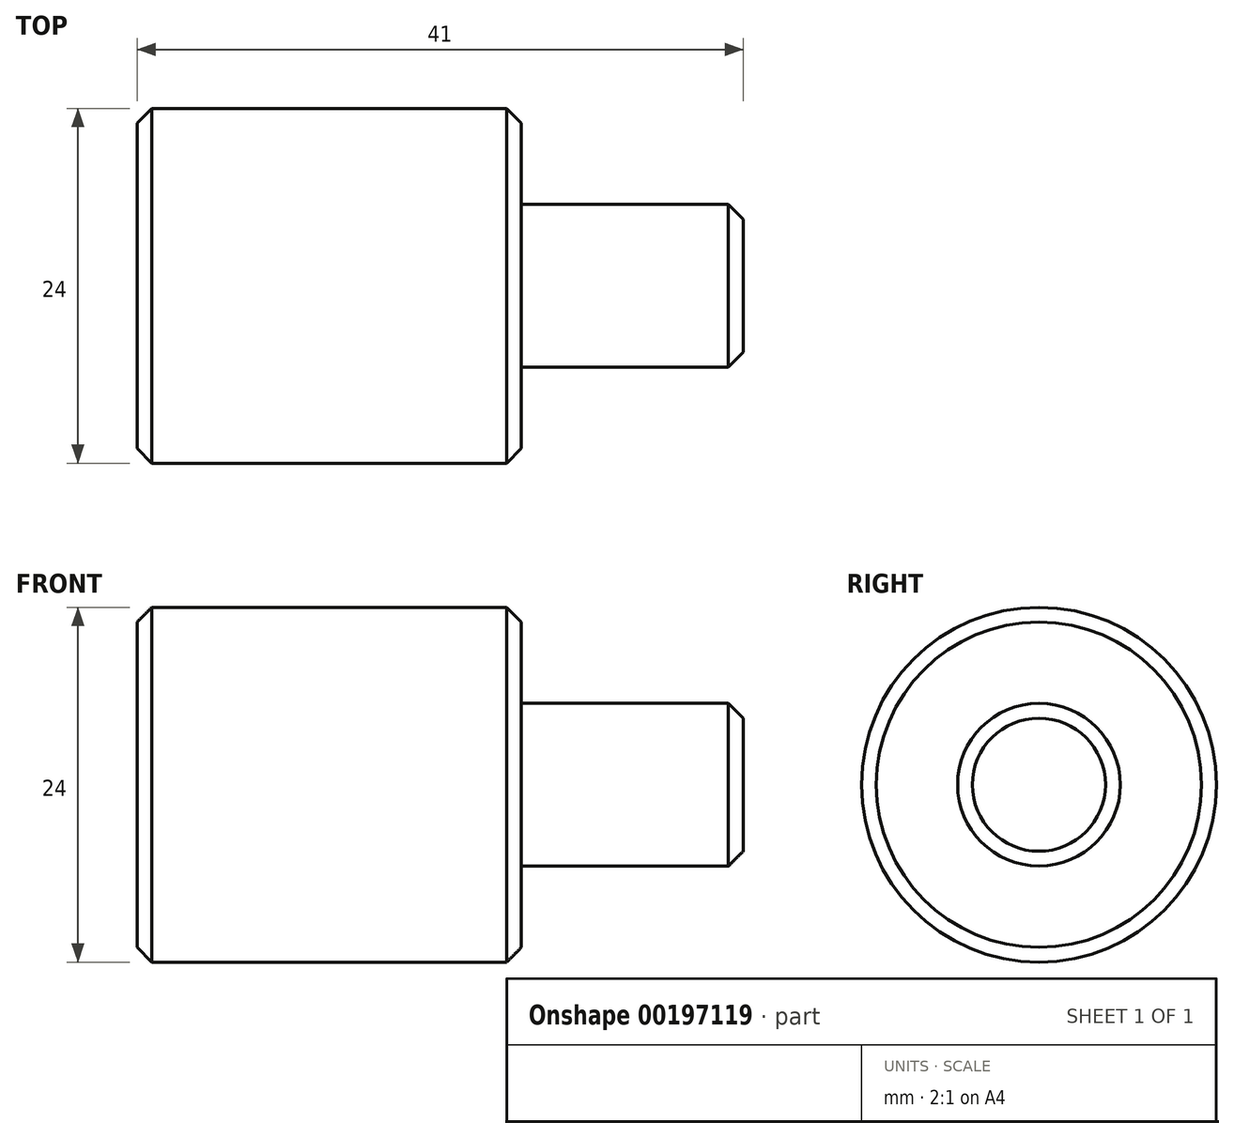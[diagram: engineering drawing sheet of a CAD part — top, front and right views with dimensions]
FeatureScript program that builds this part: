
annotation { "Feature Type Name" : "Feature", "Feature Type Description" : "" }
export const myFeature = defineFeature(function(context is Context, id is Id, definition is map)
    precondition{}
    {
        {
            var Q0;
            Q0=qCreatedBy(makeId("Front.planeOp"),FACE);
            var sketch = newSketch(context, id + "F0", { "sketchPlane" : qUnion([Q0])});
            skLineSegment(sketch, "E0", {"start": v(-12.2, 0) * mm, "end": v(50.6, 0) * mm, "construction": true});
            skLineSegment(sketch, "E1", {"start": v(0, 0) * mm, "end": v(0, 12) * mm});
            skLineSegment(sketch, "E2", {"start": v(0, 12) * mm, "end": v(26, 12) * mm});
            skLineSegment(sketch, "E3", {"start": v(26, 12) * mm, "end": v(26, 5.5) * mm});
            skLineSegment(sketch, "E4", {"start": v(26, 5.5) * mm, "end": v(41, 5.5) * mm});
            skLineSegment(sketch, "E5", {"start": v(41, 5.5) * mm, "end": v(41, 0) * mm});
            skLineSegment(sketch, "E6", {"start": v(41, 0) * mm, "end": v(0, 0) * mm});
            skSolve(sketch);
        }
        {
            var Q0;
            Q0 = qSketchRegion(id + "F0", true);
            var Q1;
            Q1=sQuery(id+"F0.wireOp",EDGE,"E0");
            revolve(context, id + "F1", {"entities" : qUnion([Q0]), "axis" : qUnion([Q1]), "revolveType" : RevolveType.FULL});
        }
        {
            var Q0;
            Q0=makeQuery(id+"F1.opRevolve","SWEPT_EDGE",EDGE,{"disambiguationData":[OSD([sQuery(id+"F0.wireOp",EDGE,"E1"),sQuery(id+"F0.wireOp",EDGE,"E2")])]});
            var Q1;
            Q1=makeQuery(id+"F1.opRevolve","SWEPT_EDGE",EDGE,{"disambiguationData":[OSD([sQuery(id+"F0.wireOp",EDGE,"E2"),sQuery(id+"F0.wireOp",EDGE,"E3")])]});
            var Q2;
            Q2=makeQuery(id+"F1.opRevolve","SWEPT_EDGE",EDGE,{"disambiguationData":[OSD([sQuery(id+"F0.wireOp",EDGE,"E4"),sQuery(id+"F0.wireOp",EDGE,"E5")])]});
            chamfer(context, id + "F2", {"entities" : qUnion([Q0, Q1, Q2]), "width" : 1 * mm, "tangentPropagation" : true});
        }
    });
